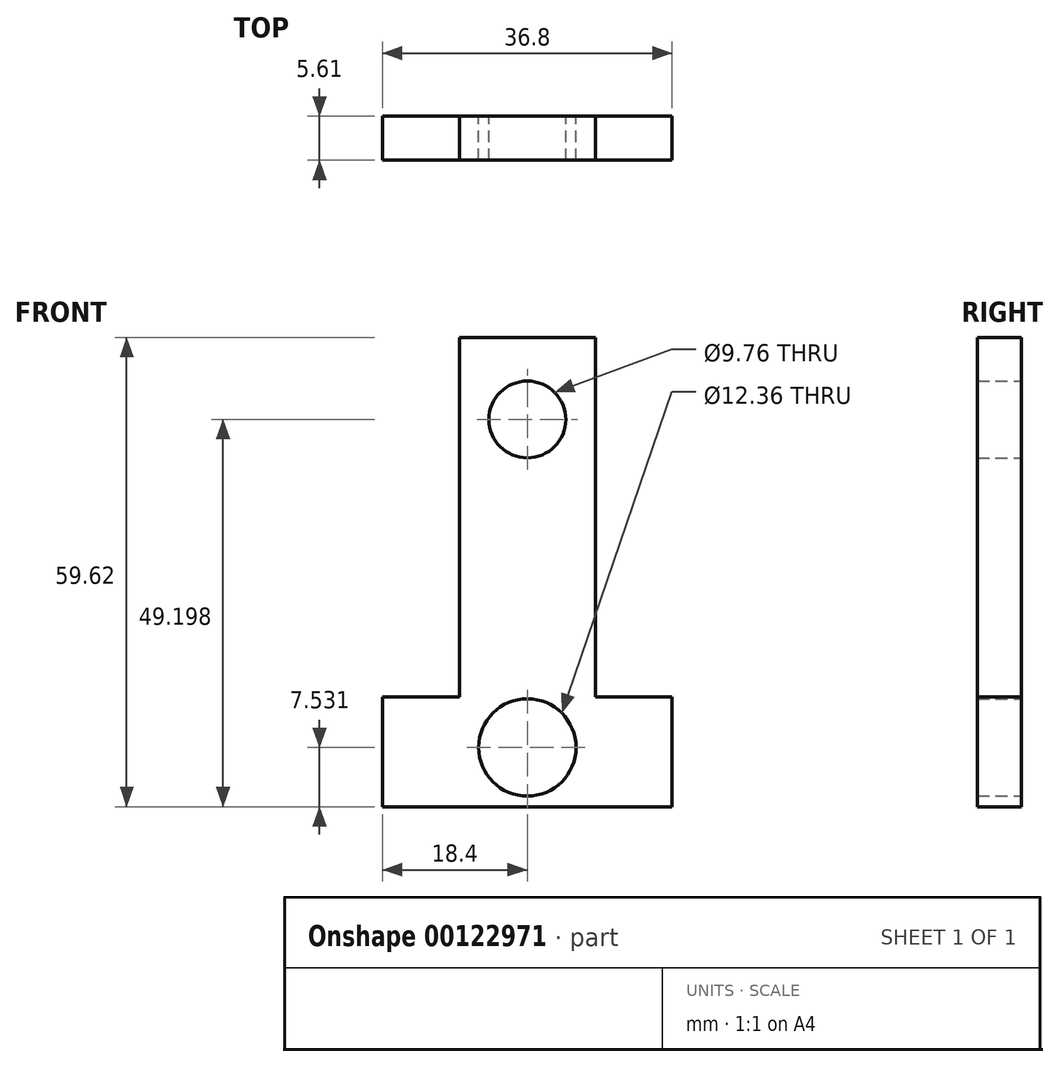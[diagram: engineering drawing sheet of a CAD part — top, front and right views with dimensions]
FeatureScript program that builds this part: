
annotation { "Feature Type Name" : "Feature", "Feature Type Description" : "" }
export const myFeature = defineFeature(function(context is Context, id is Id, definition is map)
    precondition{}
    {
        {
            var Q0;
            Q0=qCreatedBy(makeId("Front.planeOp"),FACE);
            var sketch = newSketch(context, id + "F0", { "sketchPlane" : qUnion([Q0])});
            skLineSegment(sketch, "E0", {"start": v(-8.64, 22.39) * mm, "end": v(-8.64, -23.27) * mm});
            skLineSegment(sketch, "E1", {"start": v(-8.64, -23.27) * mm, "end": v(-18.4, -23.27) * mm});
            skLineSegment(sketch, "E2", {"start": v(-18.4, -23.27) * mm, "end": v(-18.4, -37.23) * mm});
            skLineSegment(sketch, "E3", {"start": v(-18.4, -37.23) * mm, "end": v(0, -37.23) * mm});
            skLineSegment(sketch, "E4", {"start": v(-8.64, 22.39) * mm, "end": v(0, 22.39) * mm});
            skLineSegment(sketch, "E5.MirrorCS", {"start": v(8.64, 22.39) * mm, "end": v(0, 22.39) * mm});
            skLineSegment(sketch, "E6.MirrorCS", {"start": v(8.64, 22.39) * mm, "end": v(8.64, -23.27) * mm});
            skLineSegment(sketch, "E7.MirrorCS", {"start": v(8.64, -23.27) * mm, "end": v(18.4, -23.27) * mm});
            skLineSegment(sketch, "E8.MirrorCS", {"start": v(18.4, -23.27) * mm, "end": v(18.4, -37.23) * mm});
            skLineSegment(sketch, "E9.MirrorCS", {"start": v(18.4, -37.23) * mm, "end": v(0, -37.23) * mm});
            skSolve(sketch);
        }
        {
            var Q0;
            Q0=makeQuery(id+"F0.imprint","IMPRINT",FACE,{"disambiguationData":[TD([[makeQuery(id+"F0.imprint","IMPRINT",EDGE,{"derivedFrom":sQuery(id+"F0.wireOp",EDGE,"E0")}),1.0]])]});
            var sketch = newSketch(context, id + "F1", { "sketchPlane" : qUnion([Q0])});
            skCircle(sketch, "E10", {"center": v(0, -29.7) * mm, "radius": 6.18 * mm});
            skSolve(sketch);
        }
        {
            var Q0;
            Q0=makeQuery(id+"F0.imprint","IMPRINT",FACE,{"disambiguationData":[TD([[makeQuery(id+"F0.imprint","IMPRINT",EDGE,{"derivedFrom":sQuery(id+"F0.wireOp",EDGE,"E0")}),1.0]])]});
            var sketch = newSketch(context, id + "F2", { "sketchPlane" : qUnion([Q0])});
            skCircle(sketch, "E11", {"center": v(0, 11.97) * mm, "radius": 4.88 * mm});
            skSolve(sketch);
        }
        {
            var Q0;
            Q0=makeQuery(id+"F2.imprint","IMPRINT",FACE,{"disambiguationData":[TD([[makeQuery(id+"F2.imprint","IMPRINT",EDGE,{"derivedFrom":sQuery(id+"F2.wireOp",EDGE,"E11")}),-1.0]])]});
            var Q1;
            Q1=makeQuery(id+"F2.imprint","IMPRINT",FACE,{"disambiguationData":[TD([[makeQuery(id+"F2.imprint","IMPRINT",EDGE,{"derivedFrom":sQuery(id+"F2.wireOp",EDGE,"E11")}),1.0]])]});
            extrude(context, id + "F3", {"entities" : qUnion([Q0, Q1]), "depth" : 5.6 * mm});
        }
        {
            var Q0;
            Q0=makeQuery(id+"F2.imprint","IMPRINT",FACE,{"disambiguationData":[TD([[makeQuery(id+"F2.imprint","IMPRINT",EDGE,{"derivedFrom":sQuery(id+"F2.wireOp",EDGE,"E11")}),1.0]])]});
            extrude(context, id + "F4", {"entities" : qUnion([Q0]), "operationType" : NewBodyOperationType.REMOVE, "depth" : 25.4 * mm});
        }
        {
            var Q0;
            Q0=makeQuery(id+"F1.imprint","IMPRINT",FACE,{"disambiguationData":[TD([[makeQuery(id+"F1.imprint","IMPRINT",EDGE,{"derivedFrom":sQuery(id+"F1.wireOp",EDGE,"E10")}),1.0]])]});
            extrude(context, id + "F5", {"entities" : qUnion([Q0]), "operationType" : NewBodyOperationType.REMOVE, "depth" : 25.4 * mm});
        }
    });
